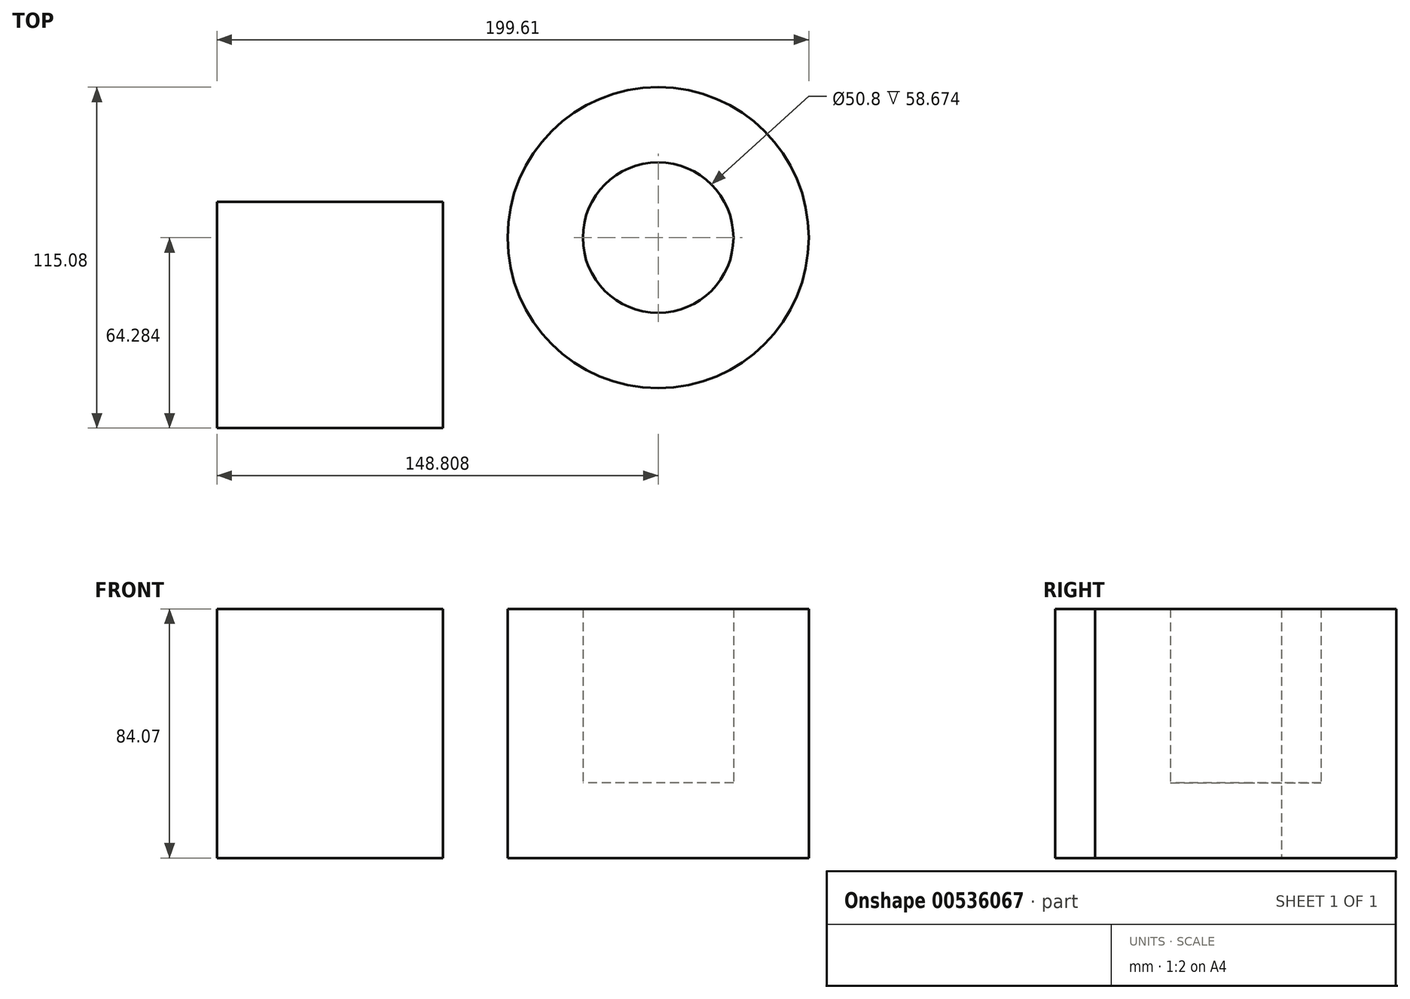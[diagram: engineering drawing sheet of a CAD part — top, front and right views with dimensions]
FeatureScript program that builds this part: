
annotation { "Feature Type Name" : "Feature", "Feature Type Description" : "" }
export const myFeature = defineFeature(function(context is Context, id is Id, definition is map)
    precondition{}
    {
        {
            var Q0;
            Q0=qCreatedBy(makeId("Top.planeOp"),FACE);
            var sketch = newSketch(context, id + "F0", { "sketchPlane" : qUnion([Q0])});
            skLineSegment(sketch, "E0.bottom", {"start": v(-116.04, 45.98) * mm, "end": v(-39.84, 45.98) * mm});
            skLineSegment(sketch, "E0.top", {"start": v(-116.04, -30.35) * mm, "end": v(-39.84, -30.35) * mm});
            skLineSegment(sketch, "E0.left", {"start": v(-116.04, 45.98) * mm, "end": v(-116.04, -30.35) * mm});
            skLineSegment(sketch, "E0.right", {"start": v(-39.84, 45.98) * mm, "end": v(-39.84, -30.35) * mm});
            skCircle(sketch, "E1", {"center": v(32.77, 33.93) * mm, "radius": 50.8 * mm});
            skSolve(sketch);
        }
        {
            var Q0;
            Q0 = qSketchRegion(id + "F0", true);
            extrude(context, id + "F1", {"entities" : qUnion([Q0]), "depth" : 84.07 * mm, "offsetDistance" : 25.4 * mm});
        }
        {
            var Q0;
            Q0=makeQuery(id+"F1.opExtrude","CAP_FACE",FACE,{"disambiguationData":[OSD([sQuery(id+"F0.wireOp",EDGE,"E1")])],"isStart":false});
            shell(context, id + "F2", {"entities" : qUnion([Q0]), "thickness" : 25.4 * mm});
        }
    });
